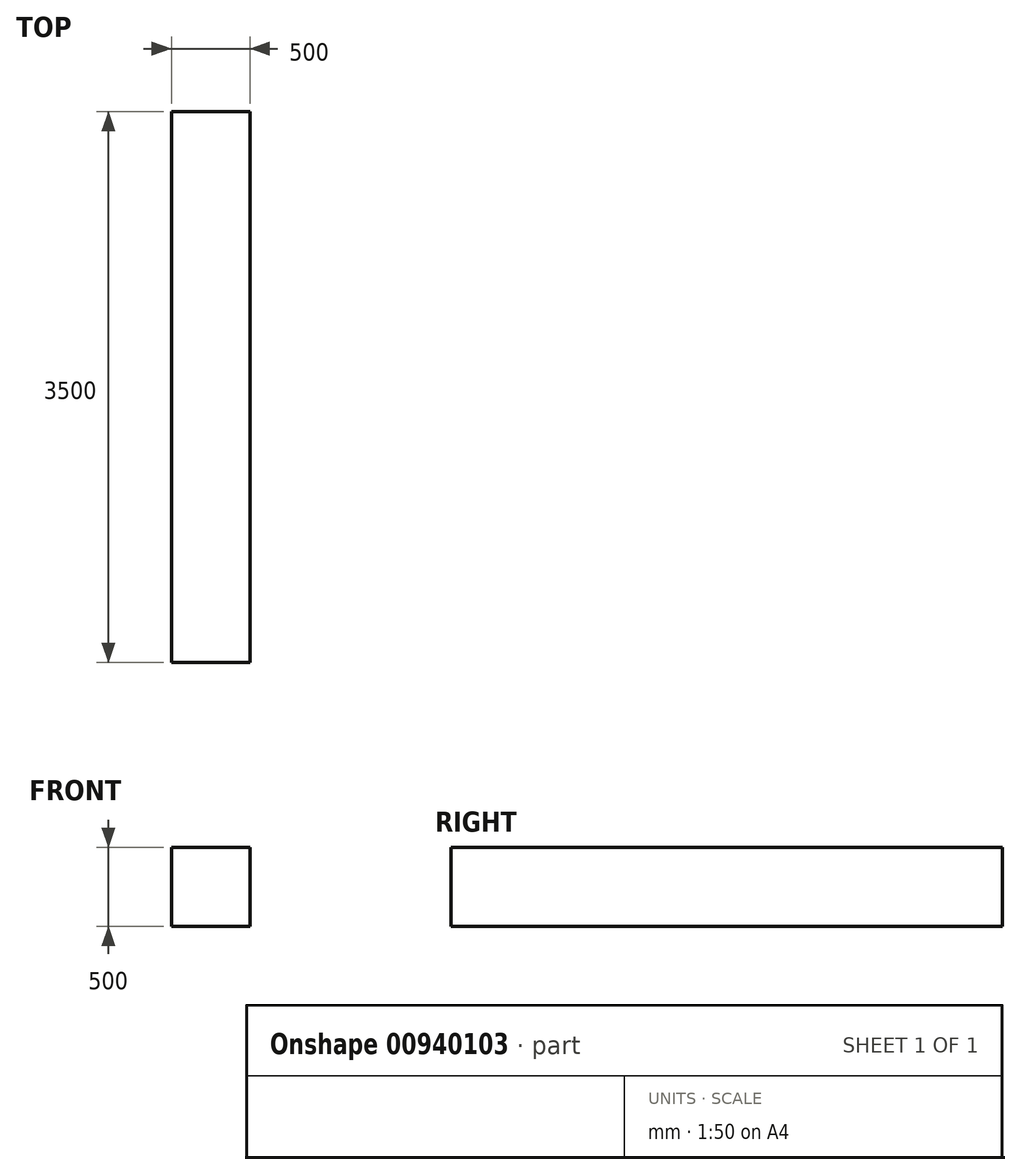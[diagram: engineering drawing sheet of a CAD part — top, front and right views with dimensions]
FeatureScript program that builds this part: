
annotation { "Feature Type Name" : "Feature", "Feature Type Description" : "" }
export const myFeature = defineFeature(function(context is Context, id is Id, definition is map)
    precondition{}
    {
        {
            var Q0;
            Q0=qCreatedBy(makeId("Front.planeOp"),FACE);
            var sketch = newSketch(context, id + "F0", { "sketchPlane" : qUnion([Q0])});
            skLineSegment(sketch, "E0.bottom", {"start": v(250, 250) * mm, "end": v(-250, 250) * mm});
            skLineSegment(sketch, "E0.top", {"start": v(250, -250) * mm, "end": v(-250, -250) * mm});
            skLineSegment(sketch, "E0.left", {"start": v(250, 250) * mm, "end": v(250, -250) * mm});
            skLineSegment(sketch, "E0.right", {"start": v(-250, 250) * mm, "end": v(-250, -250) * mm});
            skPoint(sketch, "E0.middle", {"position": v(0, 0) * mm});
            skSolve(sketch);
        }
        {
            var Q0;
            Q0=makeQuery(id+"F0.imprint","IMPRINT",FACE,{"disambiguationData":[TD([[makeQuery(id+"F0.imprint","IMPRINT",EDGE,{"derivedFrom":sQuery(id+"F0.wireOp",EDGE,"E0.bottom")}),1.0]])]});
            extrude(context, id + "F1", {"entities" : qUnion([Q0]), "depth" : 3500 * mm, "offsetDistance" : 25 * mm});
        }
    });
